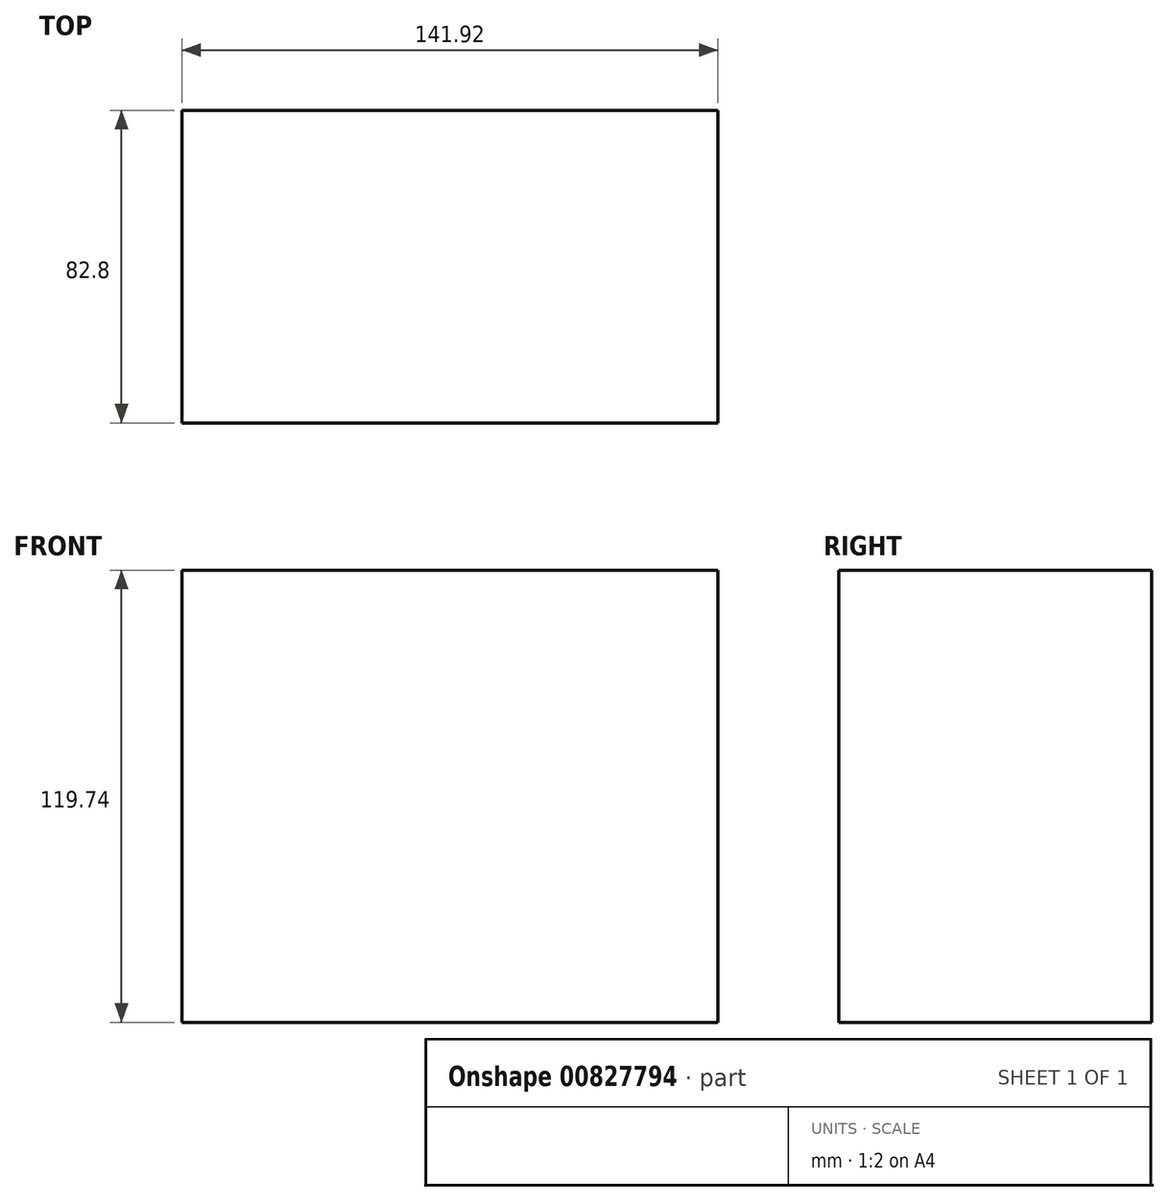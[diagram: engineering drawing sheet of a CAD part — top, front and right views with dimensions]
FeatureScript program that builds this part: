
annotation { "Feature Type Name" : "Feature", "Feature Type Description" : "" }
export const myFeature = defineFeature(function(context is Context, id is Id, definition is map)
    precondition{}
    {
        {
            var Q0;
            Q0=qCreatedBy(makeId("Front.planeOp"),FACE);
            var sketch = newSketch(context, id + "F0", { "sketchPlane" : qUnion([Q0])});
            skLineSegment(sketch, "E0.bottom", {"start": v(70.96, -59.87) * mm, "end": v(-70.96, -59.87) * mm});
            skLineSegment(sketch, "E0.top", {"start": v(70.96, 59.87) * mm, "end": v(-70.96, 59.87) * mm});
            skLineSegment(sketch, "E0.left", {"start": v(70.96, -59.87) * mm, "end": v(70.96, 59.87) * mm});
            skLineSegment(sketch, "E0.right", {"start": v(-70.96, -59.87) * mm, "end": v(-70.96, 59.87) * mm});
            skPoint(sketch, "E0.middle", {"position": v(0, 0) * mm});
            skSolve(sketch);
        }
        {
            var Q0;
            Q0 = qSketchRegion(id + "F0", true);
            extrude(context, id + "F1", {"entities" : qUnion([Q0]), "depth" : 82.8 * mm, "offsetDistance" : 25.4 * mm});
        }
    });
